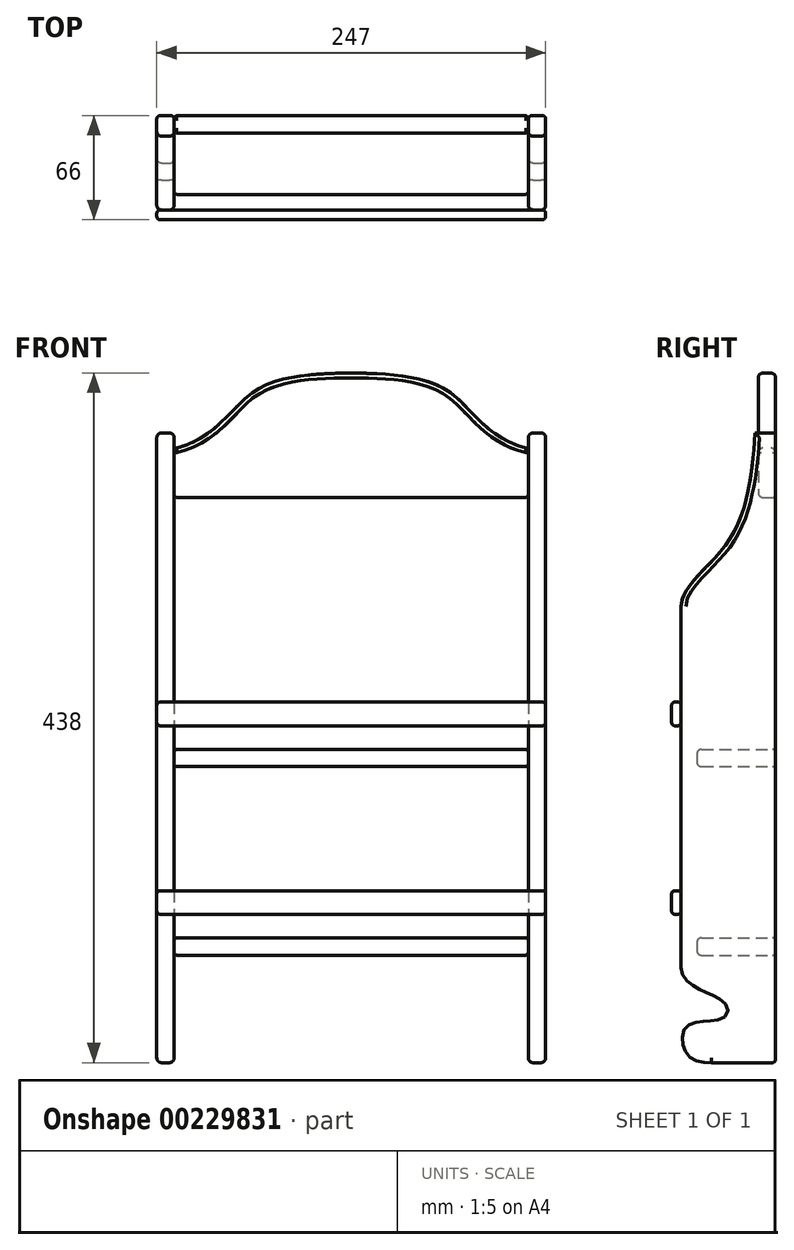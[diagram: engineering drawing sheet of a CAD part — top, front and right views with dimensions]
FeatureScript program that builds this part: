
annotation { "Feature Type Name" : "Feature", "Feature Type Description" : "" }
export const myFeature = defineFeature(function(context is Context, id is Id, definition is map)
    precondition{}
    {
        {
            assignVariable(context, id + "F0", {"name" : "Espesor", "anyValue" : 11 * mm});
        }
        {
            var Q0;
            Q0=qCreatedBy(makeId("Front.planeOp"),FACE);
            var sketch = newSketch(context, id + "F1", { "sketchPlane" : qUnion([Q0])});
            skLineSegment(sketch, "E0.bottom", {"start": v(-123.5, 109.13) * mm, "end": v(-112.5, 109.13) * mm});
            skLineSegment(sketch, "E0.top", {"start": v(-123.5, -290.87) * mm, "end": v(-112.5, -290.87) * mm});
            skLineSegment(sketch, "E0.left", {"start": v(-123.5, 109.13) * mm, "end": v(-123.5, -290.87) * mm});
            skLineSegment(sketch, "E0.right", {"start": v(-112.5, 109.13) * mm, "end": v(-112.5, -290.87) * mm});
            skLineSegment(sketch, "E1.bottom", {"start": v(-112.5, -91.86) * mm, "end": v(0, -91.86) * mm});
            skLineSegment(sketch, "E1.top", {"start": v(-112.5, -102.86) * mm, "end": v(0, -102.86) * mm});
            skLineSegment(sketch, "E1.left", {"start": v(-112.5, -91.86) * mm, "end": v(-112.5, -102.86) * mm});
            skLineSegment(sketch, "E1.right", {"start": v(0, -91.86) * mm, "end": v(0, -102.86) * mm, "construction": true});
            skLineSegment(sketch, "E2.bottom", {"start": v(-112.5, -211.63) * mm, "end": v(0, -211.63) * mm});
            skLineSegment(sketch, "E2.top", {"start": v(-112.5, -222.63) * mm, "end": v(0, -222.63) * mm});
            skLineSegment(sketch, "E2.left", {"start": v(-112.5, -211.63) * mm, "end": v(-112.5, -222.63) * mm});
            skLineSegment(sketch, "E2.right", {"start": v(0, -211.63) * mm, "end": v(0, -222.63) * mm, "construction": true});
            skLineSegment(sketch, "E3", {"start": v(-112.5, 68.13) * mm, "end": v(0, 68.13) * mm});
            skLineSegment(sketch, "E4", {"start": v(0, 68.13) * mm, "end": v(0, 147.13) * mm, "construction": true});
            skFitSpline(sketch, "E5", {"points": [v(-112.5, 99.13) * mm, v(-73.93, 124.58) * mm, v(0, 147.13) * mm], "startDerivative": vector(127.26, 29.67) * mm, "endDerivative": vector(276.23, 0) * mm});
            skLineSegment(sketch, "E6", {"start": v(0, 147.13) * mm, "end": v(-51.93, 147.13) * mm, "construction": true});
            skFitSpline(sketch, "E7.MirrorCS", {"points": [v(112.5, 99.13) * mm, v(73.93, 124.58) * mm, v(0, 147.13) * mm], "startDerivative": vector(-127.26, 29.67) * mm, "endDerivative": vector(-276.23, 0) * mm});
            skLineSegment(sketch, "E8.MirrorCS", {"start": v(112.5, 68.13) * mm, "end": v(0, 68.13) * mm});
            skLineSegment(sketch, "E9.MirrorCS", {"start": v(112.5, 109.13) * mm, "end": v(112.5, -290.87) * mm});
            skLineSegment(sketch, "E10.MirrorCS", {"start": v(123.5, 109.13) * mm, "end": v(112.5, 109.13) * mm});
            skLineSegment(sketch, "E11.MirrorCS", {"start": v(123.5, 109.13) * mm, "end": v(123.5, -290.87) * mm});
            skLineSegment(sketch, "E12.MirrorCS", {"start": v(123.5, -290.87) * mm, "end": v(112.5, -290.87) * mm});
            skLineSegment(sketch, "E13.MirrorCS", {"start": v(112.5, -222.63) * mm, "end": v(0, -222.63) * mm});
            skLineSegment(sketch, "E14.MirrorCS", {"start": v(112.5, -211.63) * mm, "end": v(0, -211.63) * mm});
            skLineSegment(sketch, "E15.MirrorCS", {"start": v(112.5, -102.86) * mm, "end": v(0, -102.86) * mm});
            skLineSegment(sketch, "E16.MirrorCS", {"start": v(112.5, -91.86) * mm, "end": v(0, -91.86) * mm});
            skSolve(sketch);
        }
        {
            var Q0;
            {var subQ0=sQuery(id+"F1.wireOp",EDGE,"E3");Q0=makeQuery(id+"F1.imprint","IMPRINT",FACE,{"disambiguationData":[TD([[makeQuery(id+"F1.imprint","IMPRINT",EDGE,{"derivedFrom":subQ0}),1.0]])]});}
            extrude(context, id + "F2", {"entities" : qUnion([Q0]), "depth" : getVariable(context, 'Espesor')});
        }
        {
            var Q0;
            {var subQ1=sQuery(id+"F1.wireOp",EDGE,"E0.bottom");Q0=makeQuery(id+"F1.imprint","IMPRINT",FACE,{"disambiguationData":[TD([[makeQuery(id+"F1.imprint","IMPRINT",EDGE,{"derivedFrom":subQ1}),-1.0]])]});}
            var Q1;
            {var subQ6=sQuery(id+"F1.wireOp",EDGE,"E10.MirrorCS");Q1=makeQuery(id+"F1.imprint","IMPRINT",FACE,{"disambiguationData":[TD([[makeQuery(id+"F1.imprint","IMPRINT",EDGE,{"derivedFrom":subQ6}),1.0]])]});}
            extrude(context, id + "F3", {"entities" : qUnion([Q0, Q1]), "depth" : 60 * mm});
        }
        {
            var Q0;
            Q0=makeQuery(id+"F1.imprint","IMPRINT",FACE,{"disambiguationData":[TD([[makeQuery(id+"F1.imprint","IMPRINT",EDGE,{"derivedFrom":sQuery(id+"F1.wireOp",EDGE,"E1.bottom")}),-1.0]])]});
            var Q1;
            Q1=makeQuery(id+"F1.imprint","IMPRINT",FACE,{"disambiguationData":[TD([[makeQuery(id+"F1.imprint","IMPRINT",EDGE,{"derivedFrom":sQuery(id+"F1.wireOp",EDGE,"E2.bottom")}),-1.0]])]});
            extrude(context, id + "F4", {"entities" : qUnion([Q0, Q1]), "depth" : 50 * mm});
        }
        {
            var Q0;
            Q0=makeQuery(id+"F3.opExtrude","SWEPT_FACE",FACE,{"disambiguationData":[OSD([sQuery(id+"F1.wireOp",EDGE,"E11.MirrorCS")])]});
            var sketch = newSketch(context, id + "F5", { "sketchPlane" : qUnion([Q0])});
            skFitSpline(sketch, "E17", {"points": [v(-13.02, 109.13) * mm, v(-29.58, 41.02) * mm, v(-60, -0.97) * mm], "startDerivative": vector(-8.36, -121.14) * mm, "endDerivative": vector(0, -88.62) * mm});
            skFitSpline(sketch, "E18", {"points": [v(-24.47, -290.87) * mm, v(-56.32, -285.3) * mm, v(-56.32, -267.56) * mm, v(-32.76, -262.29) * mm, v(-32.76, -252.57) * mm, v(-60, -230.22) * mm], "startDerivative": vector(-241.24, 0) * mm, "endDerivative": vector(0, 160) * mm});
            skLineSegment(sketch, "E19", {"start": v(-60, -0.97) * mm, "end": v(-60, -230.22) * mm});
            skLineSegment(sketch, "E20", {"start": v(-24.47, -290.87) * mm, "end": v(-24.47, -329.1) * mm});
            skLineSegment(sketch, "E21", {"start": v(-24.47, -329.1) * mm, "end": v(-100.4, -329.1) * mm});
            skLineSegment(sketch, "E22", {"start": v(-100.4, -329.1) * mm, "end": v(-100.4, 127.76) * mm});
            skLineSegment(sketch, "E23", {"start": v(-100.4, 127.76) * mm, "end": v(-13.02, 127.76) * mm});
            skLineSegment(sketch, "E24", {"start": v(-13.02, 127.76) * mm, "end": v(-13.02, 109.13) * mm});
            skSolve(sketch);
        }
        {
            var Q0;
            Q0 = qSketchRegion(id + "F5", true);
            extrude(context, id + "F6", {"entities" : qUnion([Q0]), "operationType" : NewBodyOperationType.REMOVE, "endBound" : BoundingType.THROUGH_ALL, "oppositeDirection" : true, "depth" : 25 * mm});
        }
        {
            var Q0;
            Q0=makeQuery(id+"F3.opExtrude","CAP_FACE",FACE,{"disambiguationData":[OSD([sQuery(id+"F1.wireOp",EDGE,"E0.bottom"),sQuery(id+"F1.wireOp",EDGE,"E0.top"),sQuery(id+"F1.wireOp",EDGE,"E0.left"),sQuery(id+"F1.wireOp",EDGE,"E0.right"),sQuery(id+"F1.wireOp",EDGE,"E1.left"),sQuery(id+"F1.wireOp",EDGE,"E2.left")])],"isStart":false});
            var sketch = newSketch(context, id + "F7", { "sketchPlane" : qUnion([Q0])});
            skLineSegment(sketch, "E25.bottom", {"start": v(-123.5, -61.86) * mm, "end": v(123.5, -61.86) * mm});
            skLineSegment(sketch, "E25.top", {"start": v(-123.5, -76.86) * mm, "end": v(123.5, -76.86) * mm});
            skLineSegment(sketch, "E25.left", {"start": v(-123.5, -61.86) * mm, "end": v(-123.5, -76.86) * mm});
            skLineSegment(sketch, "E25.right", {"start": v(123.5, -61.86) * mm, "end": v(123.5, -76.86) * mm});
            skLineSegment(sketch, "E26.bottom", {"start": v(-123.5, -181.63) * mm, "end": v(123.5, -181.63) * mm});
            skLineSegment(sketch, "E26.top", {"start": v(-123.5, -196.63) * mm, "end": v(123.5, -196.63) * mm});
            skLineSegment(sketch, "E26.left", {"start": v(-123.5, -181.63) * mm, "end": v(-123.5, -196.63) * mm});
            skLineSegment(sketch, "E26.right", {"start": v(123.5, -181.63) * mm, "end": v(123.5, -196.63) * mm});
            skLineSegment(sketch, "E27", {"start": v(92.53, -196.63) * mm, "end": v(92.53, -211.63) * mm, "construction": true});
            skLineSegment(sketch, "E28", {"start": v(81.2, -76.86) * mm, "end": v(81.2, -91.86) * mm, "construction": true});
            skSolve(sketch);
        }
        {
            var Q0;
            Q0 = qSketchRegion(id + "F7", true);
            extrude(context, id + "F8", {"entities" : qUnion([Q0]), "depth" : 6 * mm});
        }
        {
            var Q0;
            Q0=makeQuery(id+"F3.opExtrude","CAP_EDGE",EDGE,{"disambiguationData":[OSD([sQuery(id+"F1.wireOp",EDGE,"E0.left")])],"isStart":false});
            var Q1;
            Q1=makeQuery(id+"F3.opExtrude","CAP_EDGE",EDGE,{"disambiguationData":[OSD([sQuery(id+"F1.wireOp",EDGE,"E0.right"),sQuery(id+"F1.wireOp",EDGE,"E1.left"),sQuery(id+"F1.wireOp",EDGE,"E2.left")])],"isStart":false});
            var Q2;
            Q2=makeQuery(id+"F3.opExtrude","CAP_EDGE",EDGE,{"disambiguationData":[OSD([sQuery(id+"F1.wireOp",EDGE,"E9.MirrorCS")])],"isStart":false});
            var Q3;
            Q3=makeQuery(id+"F3.opExtrude","CAP_EDGE",EDGE,{"disambiguationData":[OSD([sQuery(id+"F1.wireOp",EDGE,"E11.MirrorCS")])],"isStart":false});
            var Q4;
            Q4=makeQuery(id+"F2.opExtrude","CAP_EDGE",EDGE,{"disambiguationData":[OSD([sQuery(id+"F1.wireOp",EDGE,"E5")])],"isStart":false});
            var Q5;
            Q5=makeQuery(id+"F2.opExtrude","CAP_EDGE",EDGE,{"disambiguationData":[OSD([sQuery(id+"F1.wireOp",EDGE,"E5")])],"isStart":true});
            var Q6;
            Q6=makeQuery(id+"F2.opExtrude","CAP_EDGE",EDGE,{"disambiguationData":[OSD([sQuery(id+"F1.wireOp",EDGE,"E3"),sQuery(id+"F1.wireOp",EDGE,"E8.MirrorCS")])],"isStart":false});
            var Q7;
            Q7=makeQuery(id+"F4.opExtrude","CAP_EDGE",EDGE,{"disambiguationData":[OSD([sQuery(id+"F1.wireOp",EDGE,"E1.top"),sQuery(id+"F1.wireOp",EDGE,"E15.MirrorCS")])],"isStart":false});
            var Q8;
            Q8=makeQuery(id+"F4.opExtrude","CAP_EDGE",EDGE,{"disambiguationData":[OSD([sQuery(id+"F1.wireOp",EDGE,"E1.bottom"),sQuery(id+"F1.wireOp",EDGE,"E16.MirrorCS")])],"isStart":false});
            var Q9;
            Q9=makeQuery(id+"F4.opExtrude","CAP_EDGE",EDGE,{"disambiguationData":[OSD([sQuery(id+"F1.wireOp",EDGE,"E2.bottom"),sQuery(id+"F1.wireOp",EDGE,"E14.MirrorCS")])],"isStart":false});
            var Q10;
            Q10=makeQuery(id+"F4.opExtrude","CAP_EDGE",EDGE,{"disambiguationData":[OSD([sQuery(id+"F1.wireOp",EDGE,"E2.top"),sQuery(id+"F1.wireOp",EDGE,"E13.MirrorCS")])],"isStart":false});
            var Q11;
            Q11=makeQuery(id+"F3.opExtrude","SWEPT_EDGE",EDGE,{"disambiguationData":[OSD([sQuery(id+"F1.wireOp",EDGE,"E9.MirrorCS"),sQuery(id+"F1.wireOp",EDGE,"E10.MirrorCS")])]});
            var Q12;
            {var subQ0=sQuery(id+"F1.wireOp",EDGE,"E10.MirrorCS");var subQ1=sQuery(id+"F1.wireOp",EDGE,"E11.MirrorCS");var subQ2=sQuery(id+"F5.wireOp",EDGE,"E17");Q12=makeQuery(id+"F6.boolean.opBoolean","COPY",EDGE,{"disambiguationData":[TD([makeQuery(id+"F3.opExtrude","SWEPT_FACE",FACE,{"disambiguationData":[OSD([sQuery(id+"F1.wireOp",EDGE,"E9.MirrorCS")])]})])],"derivedFrom":makeQuery(id+"F6.opExtrude","SWEPT_EDGE",EDGE,{"disambiguationData":[OSD([subQ0,subQ1,subQ2,sQuery(id+"F5.wireOp",EDGE,"E24")])]})});}
            var Q13;
            Q13=makeQuery(id+"F3.opExtrude","SWEPT_EDGE",EDGE,{"disambiguationData":[OSD([sQuery(id+"F1.wireOp",EDGE,"E10.MirrorCS"),sQuery(id+"F1.wireOp",EDGE,"E11.MirrorCS")])]});
            var Q14;
            Q14=makeQuery(id+"F3.opExtrude","SWEPT_EDGE",EDGE,{"disambiguationData":[OSD([sQuery(id+"F1.wireOp",EDGE,"E0.bottom"),sQuery(id+"F1.wireOp",EDGE,"E0.left")])]});
            var Q15;
            {var subQ0=sQuery(id+"F5.wireOp",EDGE,"E17");Q15=makeQuery(id+"F6.boolean.opBoolean","COPY",EDGE,{"disambiguationData":[TD([makeQuery(id+"F3.opExtrude","SWEPT_FACE",FACE,{"disambiguationData":[OSD([sQuery(id+"F1.wireOp",EDGE,"E0.bottom")])]})])],"derivedFrom":makeQuery(id+"F6.opExtrude","SWEPT_EDGE",EDGE,{"disambiguationData":[OSD([sQuery(id+"F1.wireOp",EDGE,"E10.MirrorCS"),sQuery(id+"F1.wireOp",EDGE,"E11.MirrorCS"),subQ0,sQuery(id+"F5.wireOp",EDGE,"E24")])]})});}
            var Q16;
            Q16=makeQuery(id+"F3.opExtrude","SWEPT_EDGE",EDGE,{"disambiguationData":[OSD([sQuery(id+"F1.wireOp",EDGE,"E0.bottom"),sQuery(id+"F1.wireOp",EDGE,"E0.right")])]});
            fillet(context, id + "F9", {"entities" : qUnion([Q0, Q1, Q2, Q3, Q4, Q5, Q6, Q7, Q8, Q9, Q10, Q11, Q12, Q13, Q14, Q15, Q16]), "radius" : 3 * mm, "tangentPropagation" : true, "allowEdgeOverflow" : false});
        }
        {
            var Q0;
            Q0=makeQuery(id+"F3.opExtrude","CAP_FACE",FACE,{"disambiguationData":[OSD([sQuery(id+"F1.wireOp",EDGE,"E9.MirrorCS"),sQuery(id+"F1.wireOp",EDGE,"E10.MirrorCS"),sQuery(id+"F1.wireOp",EDGE,"E11.MirrorCS"),sQuery(id+"F1.wireOp",EDGE,"E12.MirrorCS")])],"isStart":true});
            var Q1;
            Q1=makeQuery(id+"F3.opExtrude","CAP_FACE",FACE,{"disambiguationData":[OSD([sQuery(id+"F1.wireOp",EDGE,"E0.bottom"),sQuery(id+"F1.wireOp",EDGE,"E0.top"),sQuery(id+"F1.wireOp",EDGE,"E0.left"),sQuery(id+"F1.wireOp",EDGE,"E0.right"),sQuery(id+"F1.wireOp",EDGE,"E1.left"),sQuery(id+"F1.wireOp",EDGE,"E2.left")])],"isStart":true});
            var Q2;
            Q2=makeQuery(id+"F2.opExtrude","CAP_EDGE",EDGE,{"disambiguationData":[OSD([sQuery(id+"F1.wireOp",EDGE,"E3"),sQuery(id+"F1.wireOp",EDGE,"E8.MirrorCS")])],"isStart":true});
            var Q3;
            Q3=makeQuery(id+"F4.opExtrude","CAP_FACE",FACE,{"disambiguationData":[OSD([sQuery(id+"F1.wireOp",EDGE,"E2.bottom"),sQuery(id+"F1.wireOp",EDGE,"E2.top"),sQuery(id+"F1.wireOp",EDGE,"E2.left"),sQuery(id+"F1.wireOp",EDGE,"E9.MirrorCS"),sQuery(id+"F1.wireOp",EDGE,"E13.MirrorCS"),sQuery(id+"F1.wireOp",EDGE,"E14.MirrorCS")])],"isStart":true});
            var Q4;
            Q4=makeQuery(id+"F4.opExtrude","CAP_FACE",FACE,{"disambiguationData":[OSD([sQuery(id+"F1.wireOp",EDGE,"E1.bottom"),sQuery(id+"F1.wireOp",EDGE,"E1.top"),sQuery(id+"F1.wireOp",EDGE,"E1.left"),sQuery(id+"F1.wireOp",EDGE,"E9.MirrorCS"),sQuery(id+"F1.wireOp",EDGE,"E15.MirrorCS"),sQuery(id+"F1.wireOp",EDGE,"E16.MirrorCS")])],"isStart":true});
            var Q5;
            Q5=makeQuery(id+"F4.opExtrude","SWEPT_EDGE",EDGE,{"disambiguationData":[OSD([sQuery(id+"F1.wireOp",EDGE,"E0.right"),sQuery(id+"F1.wireOp",EDGE,"E1.bottom"),sQuery(id+"F1.wireOp",EDGE,"E1.left")])]});
            var Q6;
            Q6=makeQuery(id+"F4.opExtrude","SWEPT_EDGE",EDGE,{"disambiguationData":[OSD([sQuery(id+"F1.wireOp",EDGE,"E0.right"),sQuery(id+"F1.wireOp",EDGE,"E2.bottom"),sQuery(id+"F1.wireOp",EDGE,"E2.left")])]});
            var Q7;
            Q7=makeQuery(id+"F4.opExtrude","SWEPT_EDGE",EDGE,{"disambiguationData":[OSD([sQuery(id+"F1.wireOp",EDGE,"E9.MirrorCS"),sQuery(id+"F1.wireOp",EDGE,"E16.MirrorCS")])]});
            var Q8;
            Q8=makeQuery(id+"F4.opExtrude","SWEPT_EDGE",EDGE,{"disambiguationData":[OSD([sQuery(id+"F1.wireOp",EDGE,"E9.MirrorCS"),sQuery(id+"F1.wireOp",EDGE,"E14.MirrorCS")])]});
            var Q9;
            Q9=makeQuery(id+"F2.opExtrude","SWEPT_EDGE",EDGE,{"disambiguationData":[OSD([sQuery(id+"F1.wireOp",EDGE,"E0.right"),sQuery(id+"F1.wireOp",EDGE,"E3")])]});
            var Q10;
            Q10=makeQuery(id+"F2.opExtrude","SWEPT_EDGE",EDGE,{"disambiguationData":[OSD([sQuery(id+"F1.wireOp",EDGE,"E8.MirrorCS"),sQuery(id+"F1.wireOp",EDGE,"E9.MirrorCS")])]});
            fillet(context, id + "F10", {"entities" : qUnion([Q0, Q1, Q2, Q3, Q4, Q5, Q6, Q7, Q8, Q9, Q10]), "radius" : 2 * mm, "tangentPropagation" : true, "allowEdgeOverflow" : false});
        }
        {
            var Q0;
            Q0=makeQuery(id+"F8.opExtrude","CAP_FACE",FACE,{"disambiguationData":[OSD([sQuery(id+"F7.wireOp",EDGE,"E25.bottom"),sQuery(id+"F7.wireOp",EDGE,"E25.top"),sQuery(id+"F7.wireOp",EDGE,"E25.left"),sQuery(id+"F7.wireOp",EDGE,"E25.right")])],"isStart":false});
            var Q1;
            Q1=makeQuery(id+"F8.opExtrude","SWEPT_FACE",FACE,{"disambiguationData":[OSD([sQuery(id+"F7.wireOp",EDGE,"E25.left")])]});
            var Q2;
            Q2=makeQuery(id+"F8.opExtrude","CAP_FACE",FACE,{"disambiguationData":[OSD([sQuery(id+"F7.wireOp",EDGE,"E26.bottom"),sQuery(id+"F7.wireOp",EDGE,"E26.top"),sQuery(id+"F7.wireOp",EDGE,"E26.left"),sQuery(id+"F7.wireOp",EDGE,"E26.right")])],"isStart":false});
            var Q3;
            Q3=makeQuery(id+"F8.opExtrude","SWEPT_FACE",FACE,{"disambiguationData":[OSD([sQuery(id+"F7.wireOp",EDGE,"E26.left")])]});
            var Q4;
            Q4=makeQuery(id+"F8.opExtrude","SWEPT_FACE",FACE,{"disambiguationData":[OSD([sQuery(id+"F7.wireOp",EDGE,"E26.right")])]});
            var Q5;
            Q5=makeQuery(id+"F8.opExtrude","SWEPT_FACE",FACE,{"disambiguationData":[OSD([sQuery(id+"F7.wireOp",EDGE,"E25.right")])]});
            var Q6;
            Q6=makeQuery(id+"F8.opExtrude","CAP_FACE",FACE,{"disambiguationData":[OSD([sQuery(id+"F7.wireOp",EDGE,"E25.bottom"),sQuery(id+"F7.wireOp",EDGE,"E25.top"),sQuery(id+"F7.wireOp",EDGE,"E25.left"),sQuery(id+"F7.wireOp",EDGE,"E25.right")])],"isStart":true});
            var Q7;
            Q7=makeQuery(id+"F8.opExtrude","CAP_FACE",FACE,{"disambiguationData":[OSD([sQuery(id+"F7.wireOp",EDGE,"E26.bottom"),sQuery(id+"F7.wireOp",EDGE,"E26.top"),sQuery(id+"F7.wireOp",EDGE,"E26.left"),sQuery(id+"F7.wireOp",EDGE,"E26.right")])],"isStart":true});
            fillet(context, id + "F11", {"entities" : qUnion([Q0, Q1, Q2, Q3, Q4, Q5, Q6, Q7]), "radius" : 2 * mm, "tangentPropagation" : true, "allowEdgeOverflow" : false});
        }
    });
